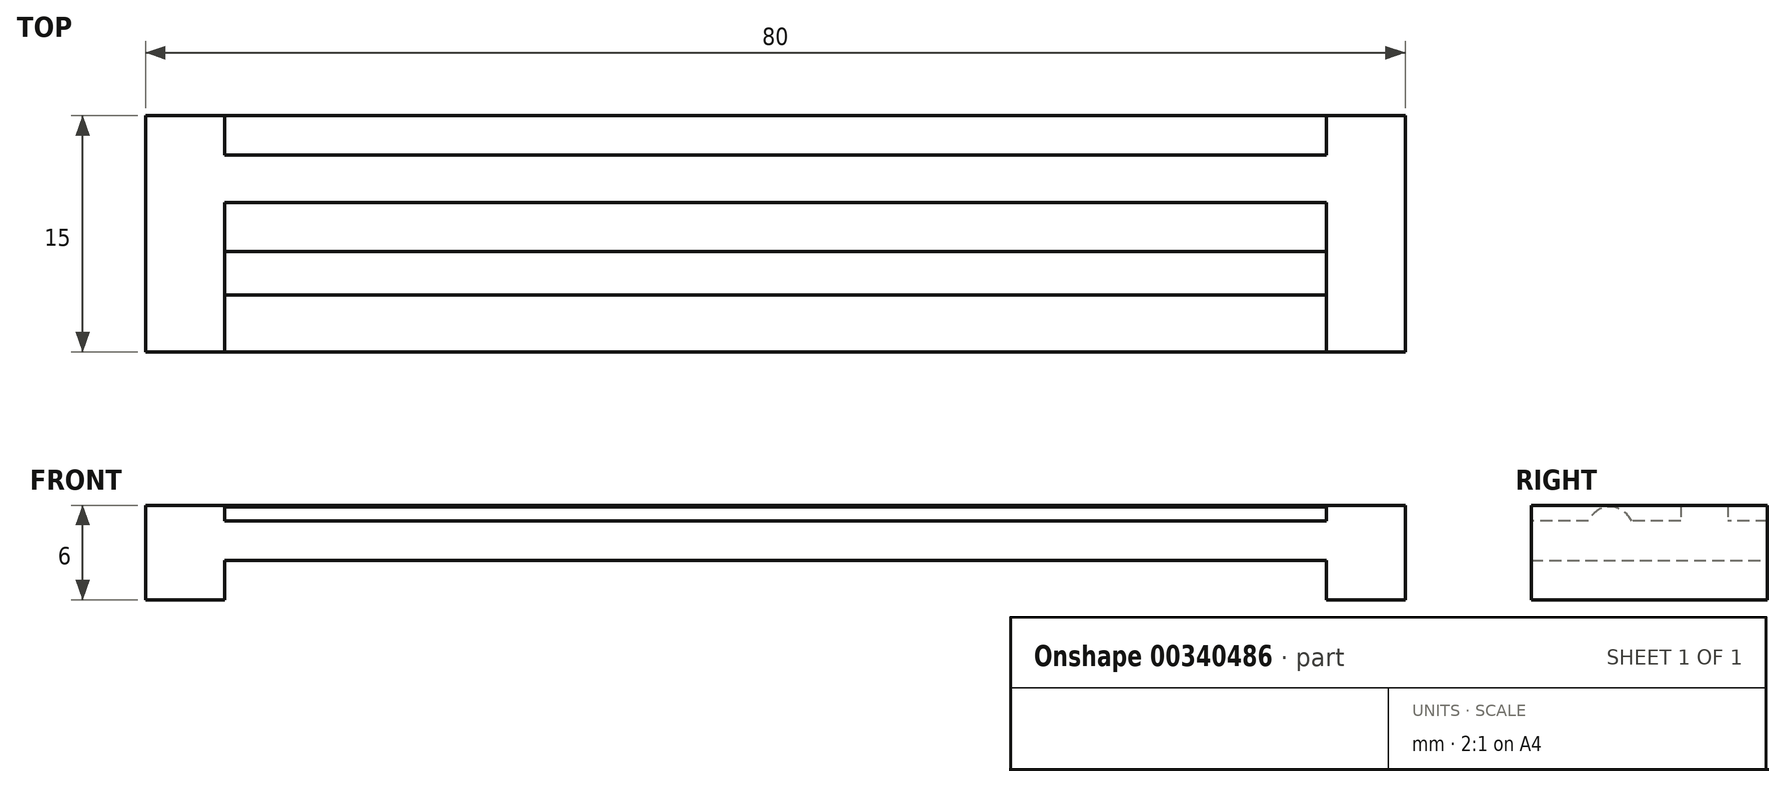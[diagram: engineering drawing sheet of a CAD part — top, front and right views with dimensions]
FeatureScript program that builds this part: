
annotation { "Feature Type Name" : "Feature", "Feature Type Description" : "" }
export const myFeature = defineFeature(function(context is Context, id is Id, definition is map)
    precondition{}
    {
        {
            var Q0;
            Q0=qCreatedBy(makeId("Top.planeOp"),FACE);
            var sketch = newSketch(context, id + "F0", { "sketchPlane" : qUnion([Q0])});
            skLineSegment(sketch, "E0.bottom", {"start": v(-40, 15) * mm, "end": v(-35, 15) * mm});
            skLineSegment(sketch, "E0.top", {"start": v(-40, 0) * mm, "end": v(-35, 0) * mm});
            skLineSegment(sketch, "E0.left", {"start": v(-40, 15) * mm, "end": v(-40, 0) * mm});
            skLineSegment(sketch, "E0.right", {"start": v(-35, 15) * mm, "end": v(-35, 0) * mm});
            skLineSegment(sketch, "E1", {"start": v(0, -67.22) * mm, "end": v(0, 65.67) * mm, "construction": true});
            skLineSegment(sketch, "E2.MirrorCS", {"start": v(40, 15) * mm, "end": v(40, 0) * mm});
            skLineSegment(sketch, "E3.MirrorCS", {"start": v(40, 15) * mm, "end": v(35, 15) * mm});
            skLineSegment(sketch, "E4.MirrorCS", {"start": v(35, 15) * mm, "end": v(35, 0) * mm});
            skLineSegment(sketch, "E5.MirrorCS", {"start": v(40, 0) * mm, "end": v(35, 0) * mm});
            skSolve(sketch);
        }
        {
            var Q0;
            Q0=makeQuery(id+"F0.imprint","IMPRINT",FACE,{"disambiguationData":[TD([[makeQuery(id+"F0.imprint","IMPRINT",EDGE,{"derivedFrom":sQuery(id+"F0.wireOp",EDGE,"E0.bottom")}),-1.0]])]});
            var Q1;
            Q1=makeQuery(id+"F0.imprint","IMPRINT",FACE,{"disambiguationData":[TD([[makeQuery(id+"F0.imprint","IMPRINT",EDGE,{"derivedFrom":sQuery(id+"F0.wireOp",EDGE,"E2.MirrorCS")}),-1.0]])]});
            extrude(context, id + "F1", {"entities" : qUnion([Q0, Q1]), "depth" : 3 * mm});
        }
        {
            var Q0;
            Q0=makeQuery(id+"F1.opExtrude","CAP_FACE",FACE,{"disambiguationData":[OSD([sQuery(id+"F0.wireOp",EDGE,"E2.MirrorCS"),sQuery(id+"F0.wireOp",EDGE,"E3.MirrorCS"),sQuery(id+"F0.wireOp",EDGE,"E4.MirrorCS"),sQuery(id+"F0.wireOp",EDGE,"E5.MirrorCS")])],"isStart":false});
            var sketch = newSketch(context, id + "F2", { "sketchPlane" : qUnion([Q0])});
            skLineSegment(sketch, "E6.bottom", {"start": v(-37.5, 12.5) * mm, "end": v(37.5, 12.5) * mm});
            skLineSegment(sketch, "E6.top", {"start": v(-37.5, 9.5) * mm, "end": v(37.5, 9.5) * mm});
            skLineSegment(sketch, "E6.left", {"start": v(-37.5, 12.5) * mm, "end": v(-37.5, 9.5) * mm});
            skLineSegment(sketch, "E6.right", {"start": v(37.5, 12.5) * mm, "end": v(37.5, 9.5) * mm});
            skSolve(sketch);
        }
        {
            var Q0;
            {var subQ0=sQuery(id+"F2.wireOp",EDGE,"E6.left");Q0=makeQuery(id+"F2.imprint","IMPRINT",FACE,{"disambiguationData":[TD([[makeQuery(id+"F2.imprint","IMPRINT",EDGE,{"derivedFrom":subQ0}),1.0]])]});}
            var Q1;
            {var subQ0=sQuery(id+"F2.wireOp",EDGE,"E6.right");Q1=makeQuery(id+"F2.imprint","IMPRINT",FACE,{"disambiguationData":[TD([[makeQuery(id+"F2.imprint","IMPRINT",EDGE,{"derivedFrom":subQ0}),-1.0]])]});}
            extrude(context, id + "F3", {"entities" : qUnion([Q0, Q1]), "depth" : 3 * mm});
        }
        {
            var Q0;
            Q0=makeQuery(id+"F3.opExtrude","SWEPT_FACE",FACE,{"disambiguationData":[OSD([sQuery(id+"F2.wireOp",EDGE,"E6.left")])]});
            var sketch = newSketch(context, id + "F4", { "sketchPlane" : qUnion([Q0])});
            skCircle(sketch, "E7", {"center": v(-5, 4.4) * mm, "radius": 1.5 * mm});
            skSolve(sketch);
        }
        {
            var Q0;
            Q0=makeQuery(id+"F4.imprint","IMPRINT",FACE,{"disambiguationData":[TD([[makeQuery(id+"F4.imprint","IMPRINT",EDGE,{"derivedFrom":sQuery(id+"F4.wireOp",EDGE,"E7")}),1.0]])]});
            extrude(context, id + "F5", {"entities" : qUnion([Q0]), "oppositeDirection" : true, "depth" : 75 * mm});
        }
        {
            var Q0;
            Q0=makeQuery(id+"F1.opExtrude","CAP_FACE",FACE,{"disambiguationData":[OSD([sQuery(id+"F0.wireOp",EDGE,"E0.bottom"),sQuery(id+"F0.wireOp",EDGE,"E0.top"),sQuery(id+"F0.wireOp",EDGE,"E0.left"),sQuery(id+"F0.wireOp",EDGE,"E0.right")])],"isStart":false});
            var Q1;
            Q1=makeQuery(id+"F3.opExtrude","CAP_FACE",FACE,{"disambiguationData":[OSD([sQuery(id+"F2.wireOp",EDGE,"E6.bottom"),sQuery(id+"F2.wireOp",EDGE,"E6.top"),sQuery(id+"F2.wireOp",EDGE,"E6.left"),sQuery(id+"F2.wireOp",EDGE,"E6.right")])],"isStart":false});
            extrude(context, id + "F6", {"entities" : qUnion([Q0]), "operationType" : NewBodyOperationType.ADD, "endBound" : BoundingType.UP_TO_SURFACE, "endBoundEntityFace" : qUnion([Q1]), "depth" : 25 * mm});
        }
        {
            var Q0;
            Q0=makeQuery(id+"F1.opExtrude","CAP_FACE",FACE,{"disambiguationData":[OSD([sQuery(id+"F0.wireOp",EDGE,"E2.MirrorCS"),sQuery(id+"F0.wireOp",EDGE,"E3.MirrorCS"),sQuery(id+"F0.wireOp",EDGE,"E4.MirrorCS"),sQuery(id+"F0.wireOp",EDGE,"E5.MirrorCS")])],"isStart":false});
            var Q1;
            Q1=makeQuery(id+"F3.opExtrude","CAP_FACE",FACE,{"disambiguationData":[OSD([sQuery(id+"F2.wireOp",EDGE,"E6.bottom"),sQuery(id+"F2.wireOp",EDGE,"E6.top"),sQuery(id+"F2.wireOp",EDGE,"E6.left"),sQuery(id+"F2.wireOp",EDGE,"E6.right")])],"isStart":false});
            extrude(context, id + "F7", {"entities" : qUnion([Q0]), "operationType" : NewBodyOperationType.ADD, "endBound" : BoundingType.UP_TO_SURFACE, "endBoundEntityFace" : qUnion([Q1]), "depth" : 25 * mm});
        }
        {
            var Q0;
            Q0 = qSketchRegion(id + "F0", true);
            extrude(context, id + "F8", {"entities" : qUnion([Q0]), "depth" : 5 * mm});
        }
        {
            var Q0;
            Q0=makeQuery(id+"F8.opExtrude","SWEPT_FACE",FACE,{"disambiguationData":[OSD([sQuery(id+"F0.wireOp",EDGE,"E0.right")])]});
            var sketch = newSketch(context, id + "F9", { "sketchPlane" : qUnion([Q0])});
            skLineSegment(sketch, "E8.bottom", {"start": v(0, 5) * mm, "end": v(15, 5) * mm});
            skLineSegment(sketch, "E8.top", {"start": v(0, 2.5) * mm, "end": v(15, 2.5) * mm});
            skLineSegment(sketch, "E8.left", {"start": v(0, 5) * mm, "end": v(0, 2.5) * mm});
            skLineSegment(sketch, "E8.right", {"start": v(15, 5) * mm, "end": v(15, 2.5) * mm});
            skSolve(sketch);
        }
        {
            var Q0;
            Q0=makeQuery(id+"F9.imprint","IMPRINT",FACE,{"disambiguationData":[TD([[makeQuery(id+"F9.imprint","IMPRINT",EDGE,{"derivedFrom":sQuery(id+"F9.wireOp",EDGE,"E8.bottom")}),1.0]])]});
            var Q1;
            Q1=makeQuery(id+"F8.opExtrude","SWEPT_BODY",BODY,{"disambiguationData":[OSD([sQuery(id+"F0.wireOp",EDGE,"E2.MirrorCS"),sQuery(id+"F0.wireOp",EDGE,"E3.MirrorCS"),sQuery(id+"F0.wireOp",EDGE,"E4.MirrorCS"),sQuery(id+"F0.wireOp",EDGE,"E5.MirrorCS")])]});
            extrude(context, id + "F10", {"entities" : qUnion([Q0]), "operationType" : NewBodyOperationType.ADD, "endBound" : BoundingType.UP_TO_BODY, "endBoundEntityBody" : qUnion([Q1]), "depth" : 25 * mm});
        }
    });
